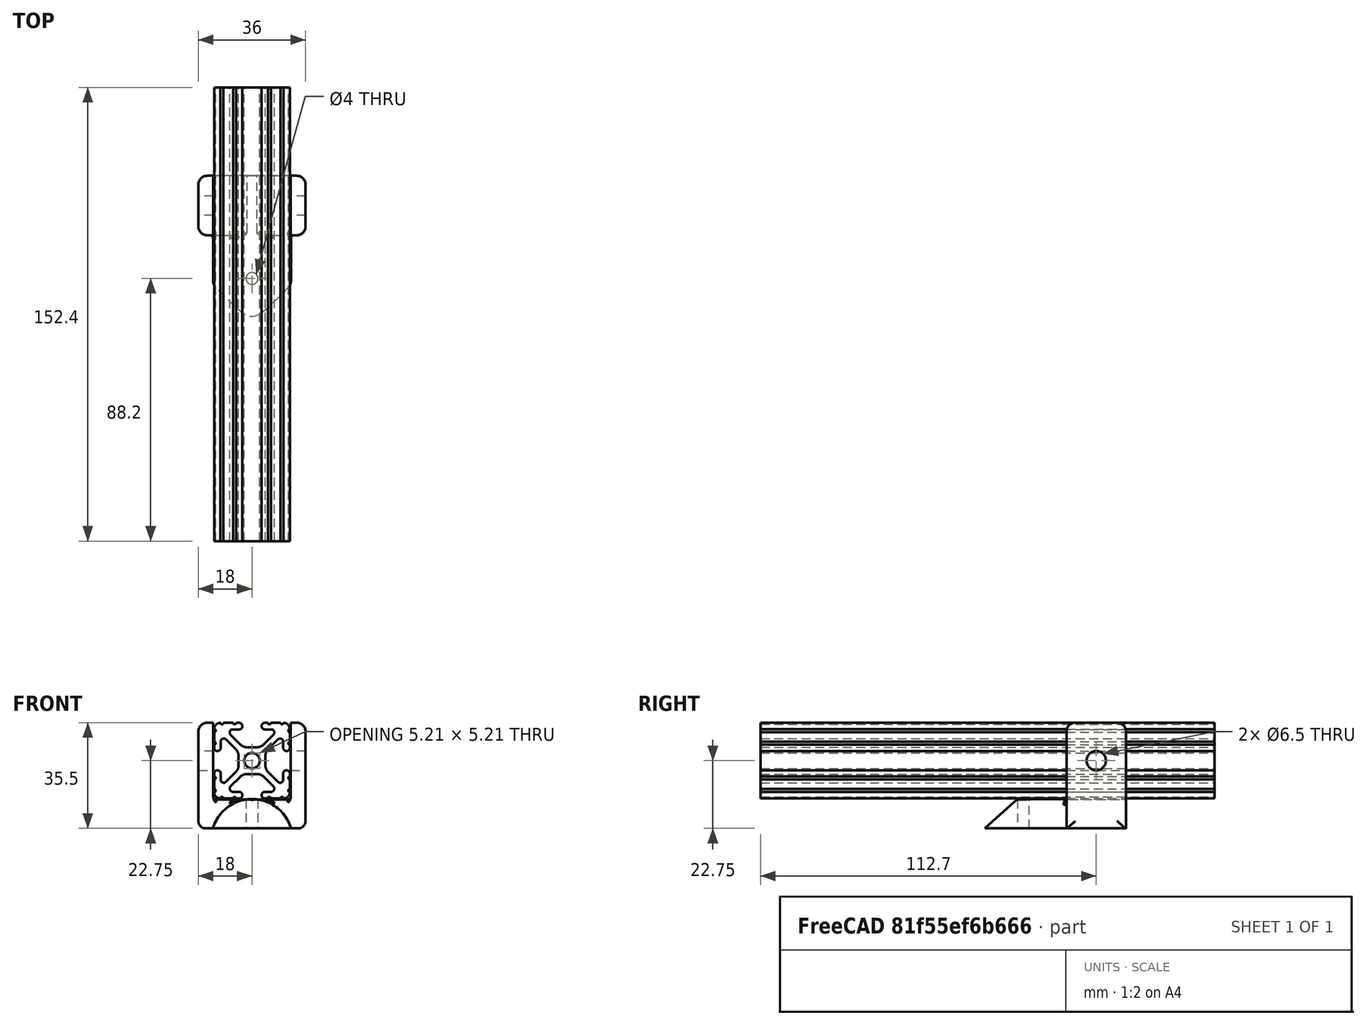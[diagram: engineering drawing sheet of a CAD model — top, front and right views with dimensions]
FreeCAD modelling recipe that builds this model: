
FCSTD DOCUMENT  (FreeCAD 0.20R29410 (Git))
Label: airModuleHolder12_05_2022
License: All rights reserved
LicenseURL: http://en.wikipedia.org/wiki/All_rights_reserved
objects: Part::Cut×6, Part::Cylinder×5, Part::Box×5, Part::Fillet×5, Part::MultiFuse×3, Part::Cone×1, Part::Feature×1
note: 26 computed .brp shape members not serialized (recipe doc carries the construction recipe); baked Part::Feature solids carry a one-line shape summary decoded from their .brp

FEATURE [Part::Cylinder] Cylinder
  Angle = 360
  AttacherType = Attacher::AttachEngine3D
  FirstAngle = 0
  Height = 36.5
  Placement = pos=(13.5,47.5,43) rot=(0,0.707107,-0.707107;3.14159rad)
  Radius = 13.6
  SecondAngle = 0
FEATURE [Part::Box] Box015  label="TSlotMount001"
  AttacherType = Attacher::AttachEngine3D
  Height = 35.5
  Length = 36
  Placement = pos=(-4.5,27.5,46.75) rot=(0,0,1;0rad)
  Width = 20
FEATURE [Part::Cylinder] Cylinder009  label="m5Cut"
  Angle = 360
  AttacherType = Attacher::AttachEngine3D
  FirstAngle = 0
  Height = 100
  Placement = pos=(-57.4,37.5,69.5) rot=(0,1,0;1.5708rad)
  Radius = 3.25
  SecondAngle = 0
FEATURE [Part::Box] Box016  label="Shell_Holder002"
  AttacherType = Attacher::AttachEngine3D
  Height = 20
  Length = 29
  Placement = pos=(-1,-20.5,26.75) rot=(0,0,1;0rad)
  Width = 75
FEATURE [Part::Box] Box018  label="TSlotFrameCut001"
  AttacherType = Attacher::AttachEngine3D
  Height = 28.5
  Length = 26
  Placement = pos=(0.5,0,56.5) rot=(0,0,1;0rad)
  Width = 254
FEATURE [Part::Cut] Cut009  label="TSlotMount002"
  Base = -> Box015
  Tool = -> Box018
FEATURE [Part::Cylinder] Cylinder015
  Angle = 360
  AttacherType = Attacher::AttachEngine3D
  FirstAngle = 0
  Height = 12
  Placement = pos=(13.5,13,45) rot=(0,0,1;1.5708rad)
  Radius = 2
  SecondAngle = 0
FEATURE [Part::Cone] Cone
  Angle = 180
  AttacherType = Attacher::AttachEngine3D
  Height = 15
  Placement = pos=(13.5,11,43) rot=(1,0,0;1.5708rad)
  Radius1 = 13.6
  Radius2 = 0
FEATURE [Part::MultiFuse] Fusion  label="beak"
  Shapes = -> [Cylinder,Cone]
FEATURE [Part::Cut] Cut
  Base = -> Fusion
  Tool = -> Box016
FEATURE [Part::Cut] Cut010
  Base = -> Cut009
  Tool = -> Cylinder009
FEATURE [Part::MultiFuse] Fusion002
  Shapes = -> [Cut,Cut010]
FEATURE [Part::Feature] Part__Feature  label="47065T801_T-Slotted Framing"
  Placement = pos=(13.5,1,69.5) rot=(1,0,0;1.5708rad)
  shape: bbox 25.4 x 152.4 x 25.4 mm, 108 faces (baked)
FEATURE [Part::Cylinder] Cylinder016
  Angle = 90
  AttacherType = Attacher::AttachEngine3D
  FirstAngle = 0
  Height = 50
  Placement = pos=(-2,50,49.25) rot=(0,0.707107,-0.707107;3.14159rad)
  Radius = 2.5
  SecondAngle = 0
FEATURE [Part::Box] Box019  label="Cube"
  AttacherType = Attacher::AttachEngine3D
  Height = 2.5
  Length = 2.5
  Placement = pos=(-4.5,0,46.75) rot=(0,0,1;0rad)
  Width = 50
FEATURE [Part::Cut] Cut012
  Base = -> Box019
  Tool = -> Cylinder016
FEATURE [Part::Box] Box020  label="Cube001"
  AttacherType = Attacher::AttachEngine3D
  Height = 2.5
  Length = 2.5
  Placement = pos=(-4.5,0,46.75) rot=(0,0,1;0rad)
  Width = 50
FEATURE [Part::Cylinder] Cylinder017
  Angle = 90
  AttacherType = Attacher::AttachEngine3D
  FirstAngle = 0
  Height = 50
  Placement = pos=(-2,50,49.25) rot=(0,0.707107,-0.707107;3.14159rad)
  Radius = 2.5
  SecondAngle = 0
FEATURE [Part::Cut] Cut013
  Base = -> Box020
  Placement = pos=(78.25,0,51.25) rot=(0,-1,0;1.5708rad)
  Tool = -> Cylinder017
FEATURE [Part::Fillet] Fillet
  Base = -> Fusion002
  Edges = 6 edges r=1: [Edge26,Edge28,Edge36,Edge38,Edge44,Edge46]
FEATURE [Part::Fillet] Fillet001
  Base = -> Fillet
  Edges = 2 edges r=3: [Edge4,Edge26]
FEATURE [Part::Fillet] Fillet002
  Base = -> Fillet001
  Edges = 2 edges r=3: [Edge48,Edge71]
FEATURE [Part::Fillet] Fillet003
  Base = -> Fillet002
  Edges = 1 edges r=3: [Edge57]
FEATURE [Part::Fillet] Fillet004
  Base = -> Fillet003
  Edges = 2 edges r=3: [Edge60,Edge73]
FEATURE [Part::MultiFuse] Fusion003  label="cuts"
  Shapes = -> [Cut013,Cut012,Cylinder015]
FEATURE [Part::Cut] Cut014
  Base = -> Fillet004
  Tool = -> Fusion003
